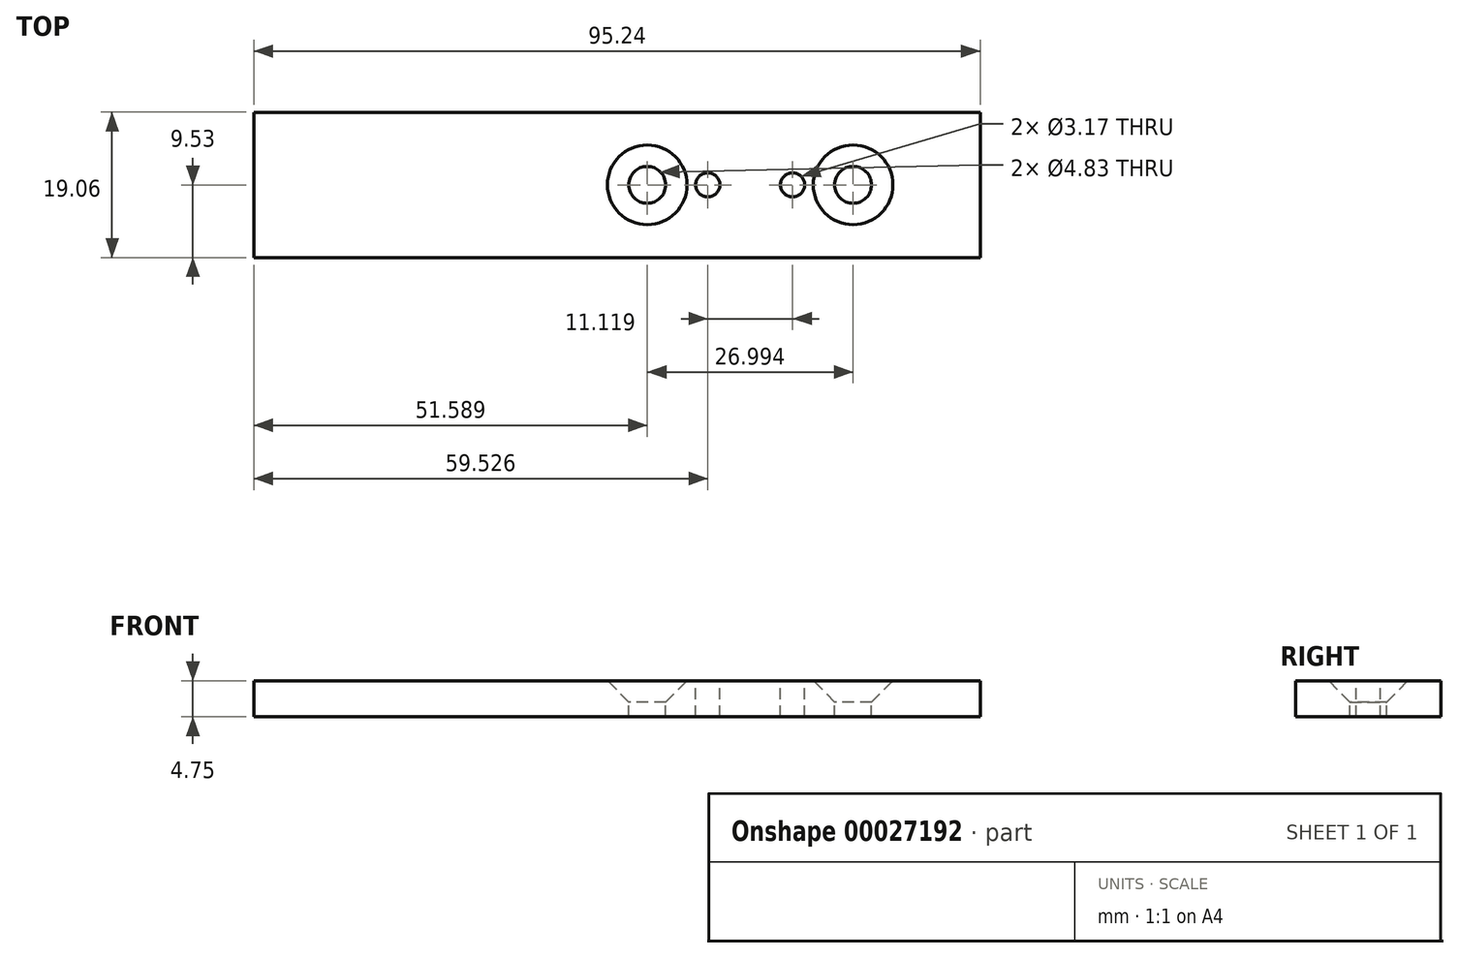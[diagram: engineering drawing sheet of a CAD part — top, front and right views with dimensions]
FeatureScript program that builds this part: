
annotation { "Feature Type Name" : "Feature", "Feature Type Description" : "" }
export const myFeature = defineFeature(function(context is Context, id is Id, definition is map)
    precondition{}
    {
        {
            var Q0;
            Q0=qCreatedBy(makeId("Top.planeOp"),FACE);
            var sketch = newSketch(context, id + "F0", { "sketchPlane" : qUnion([Q0])});
            skLineSegment(sketch, "E0.bottom", {"start": v(-47.63, 9.53) * mm, "end": v(47.63, 9.53) * mm});
            skLineSegment(sketch, "E0.top", {"start": v(-47.63, -9.53) * mm, "end": v(47.63, -9.53) * mm});
            skLineSegment(sketch, "E0.left", {"start": v(-47.63, 9.53) * mm, "end": v(-47.63, -9.53) * mm});
            skLineSegment(sketch, "E0.right", {"start": v(47.63, 9.53) * mm, "end": v(47.63, -9.53) * mm});
            skPoint(sketch, "E0.middle", {"position": v(0, 0) * mm});
            skSolve(sketch);
        }
        {
            var Q0;
            Q0=makeQuery(id+"F0.imprint","IMPRINT",FACE,{"disambiguationData":[TD([[makeQuery(id+"F0.imprint","IMPRINT",EDGE,{"derivedFrom":sQuery(id+"F0.wireOp",EDGE,"E0.bottom")}),-1.0]])]});
            extrude(context, id + "F1", {"entities" : qUnion([Q0]), "oppositeDirection" : true, "depth" : 4.75 * mm});
        }
        {
            var Q0;
            Q0=makeQuery(id+"F1.opExtrude","CAP_FACE",FACE,{"disambiguationData":[OSD([sQuery(id+"F0.wireOp",EDGE,"E0.bottom"),sQuery(id+"F0.wireOp",EDGE,"E0.top"),sQuery(id+"F0.wireOp",EDGE,"E0.left"),sQuery(id+"F0.wireOp",EDGE,"E0.right")])],"isStart":true});
            var sketch = newSketch(context, id + "F2", { "sketchPlane" : qUnion([Q0])});
            skLineSegment(sketch, "E1.0", {"start": v(41.28, 3.18) * mm, "end": v(-41.28, 3.18) * mm});
            skLineSegment(sketch, "E1.1", {"start": v(41.28, -3.18) * mm, "end": v(41.28, 3.18) * mm});
            skLineSegment(sketch, "E1.2", {"start": v(-41.28, -3.18) * mm, "end": v(41.28, -3.18) * mm});
            skLineSegment(sketch, "E1.3", {"start": v(-41.28, 3.18) * mm, "end": v(-41.28, -3.18) * mm});
            skPoint(sketch, "E2", {"position": v(3.97, 0) * mm});
            skPoint(sketch, "E3", {"position": v(11.9, 0) * mm});
            skPoint(sketch, "E4", {"position": v(23.03, 0) * mm});
            skPoint(sketch, "E5", {"position": v(30.96, 0) * mm});
            skSolve(sketch);
        }
        {
            var Q0;
            Q0=sQuery(id+"F2.wireOp",VERTEX,"E3");
            var Q1;
            Q1=sQuery(id+"F2.wireOp",VERTEX,"E4");
            var Q2;
            Q2=makeQuery(id+"F1.opExtrude","SWEPT_BODY",BODY,{"disambiguationData":[OSD([sQuery(id+"F0.wireOp",EDGE,"E0.bottom"),sQuery(id+"F0.wireOp",EDGE,"E0.top"),sQuery(id+"F0.wireOp",EDGE,"E0.left"),sQuery(id+"F0.wireOp",EDGE,"E0.right")])]});
            hole(context, id + "F3", {"style" : HoleStyle.SIMPLE, "endStyle" : HoleEndStyle.THROUGH, "holeDiameter" : 3.17 * mm, "locations" : qUnion([Q0, Q1]), "scope" : qUnion([Q2]), "isTappedThrough" : true});
        }
        {
            var Q0;
            Q0=sQuery(id+"F2.wireOp",VERTEX,"E2");
            var Q1;
            Q1=sQuery(id+"F2.wireOp",VERTEX,"E5");
            var Q2;
            Q2=makeQuery(id+"F1.opExtrude","SWEPT_BODY",BODY,{"disambiguationData":[OSD([sQuery(id+"F0.wireOp",EDGE,"E0.bottom"),sQuery(id+"F0.wireOp",EDGE,"E0.top"),sQuery(id+"F0.wireOp",EDGE,"E0.left"),sQuery(id+"F0.wireOp",EDGE,"E0.right")])]});
            hole(context, id + "F4", {"style" : HoleStyle.C_SINK, "endStyle" : HoleEndStyle.THROUGH, "holeDiameter" : 4.83 * mm, "cSinkDiameter" : 10.44 * mm, "cSinkAngle" : 90 * degree, "locations" : qUnion([Q0, Q1]), "scope" : qUnion([Q2]), "isTappedThrough" : true});
        }
    });
